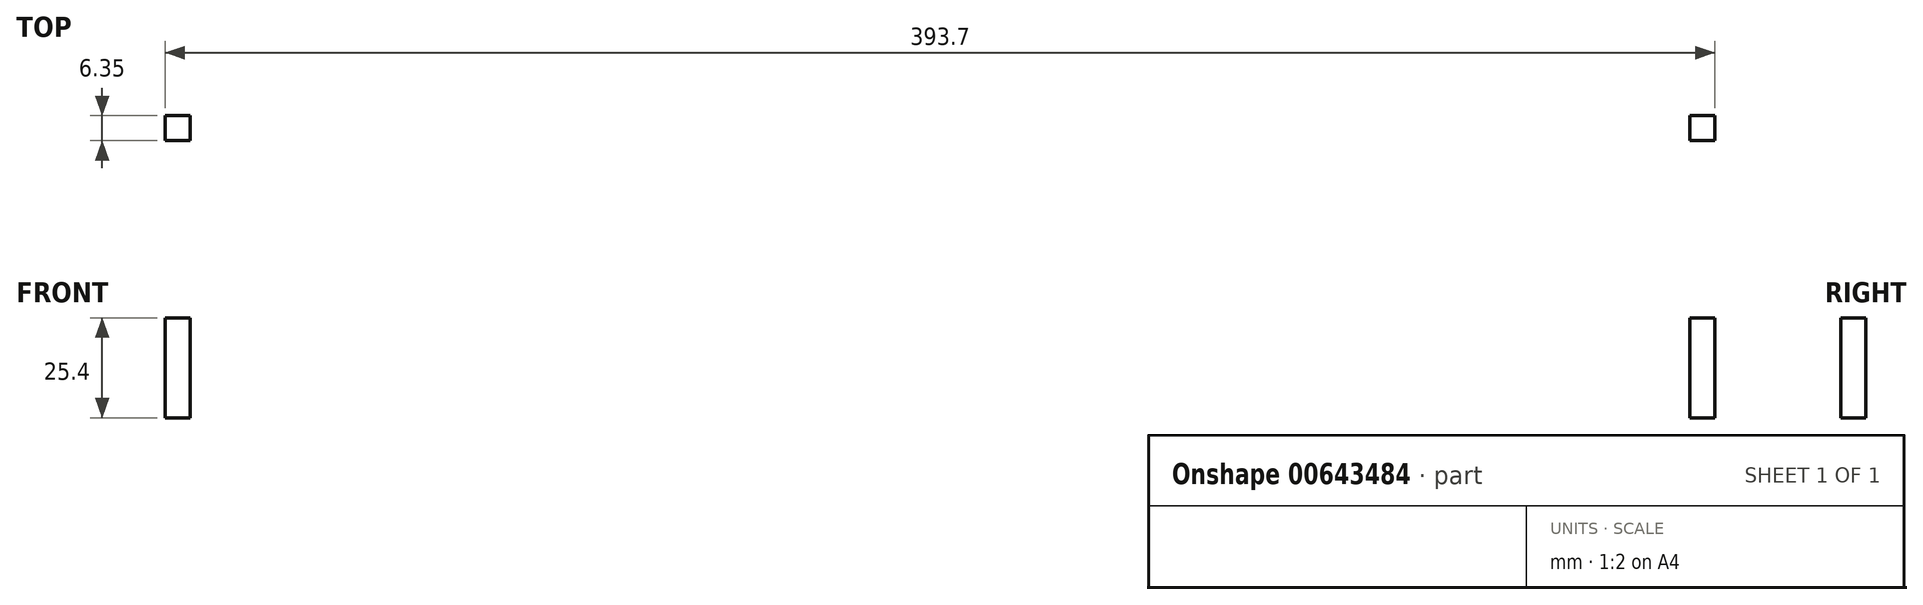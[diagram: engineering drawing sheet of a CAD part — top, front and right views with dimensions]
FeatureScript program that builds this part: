
annotation { "Feature Type Name" : "Feature", "Feature Type Description" : "" }
export const myFeature = defineFeature(function(context is Context, id is Id, definition is map)
    precondition{}
    {
        {
            var Q0;
            Q0=qCreatedBy(makeId("Front.planeOp"),FACE);
            var sketch = newSketch(context, id + "F0", { "sketchPlane" : qUnion([Q0])});
            skLineSegment(sketch, "E0.bottom", {"start": v(-181.53, -108.15) * mm, "end": v(199.47, -108.15) * mm});
            skLineSegment(sketch, "E0.top", {"start": v(-181.53, -44.65) * mm, "end": v(199.47, -44.65) * mm});
            skLineSegment(sketch, "E0.left", {"start": v(-181.53, -108.15) * mm, "end": v(-181.53, -44.65) * mm});
            skLineSegment(sketch, "E0.right", {"start": v(199.47, -108.15) * mm, "end": v(199.47, -44.65) * mm});
            skLineSegment(sketch, "E1.bottom", {"start": v(-181.53, -63.7) * mm, "end": v(-187.88, -63.7) * mm});
            skLineSegment(sketch, "E1.top", {"start": v(-181.53, -89.1) * mm, "end": v(-187.88, -89.1) * mm});
            skLineSegment(sketch, "E1.left", {"start": v(-181.53, -63.7) * mm, "end": v(-181.53, -89.1) * mm});
            skLineSegment(sketch, "E1.right", {"start": v(-187.88, -63.7) * mm, "end": v(-187.88, -89.1) * mm});
            skLineSegment(sketch, "E2.bottom", {"start": v(199.47, -63.7) * mm, "end": v(205.82, -63.7) * mm});
            skLineSegment(sketch, "E2.top", {"start": v(199.47, -89.1) * mm, "end": v(205.82, -89.1) * mm});
            skLineSegment(sketch, "E2.left", {"start": v(199.47, -63.7) * mm, "end": v(199.47, -89.1) * mm});
            skLineSegment(sketch, "E2.right", {"start": v(205.82, -63.7) * mm, "end": v(205.82, -89.1) * mm});
            skLineSegment(sketch, "E3.bottom", {"start": v(-130.73, -108.15) * mm, "end": v(-79.93, -108.15) * mm});
            skLineSegment(sketch, "E3.top", {"start": v(-130.73, -114.5) * mm, "end": v(-79.93, -114.5) * mm});
            skLineSegment(sketch, "E3.left", {"start": v(-130.73, -108.15) * mm, "end": v(-130.73, -114.5) * mm});
            skLineSegment(sketch, "E3.right", {"start": v(-79.93, -108.15) * mm, "end": v(-79.93, -114.5) * mm});
            skLineSegment(sketch, "E4.bottom", {"start": v(97.87, -108.15) * mm, "end": v(148.67, -108.15) * mm});
            skLineSegment(sketch, "E4.top", {"start": v(97.87, -114.5) * mm, "end": v(148.67, -114.5) * mm});
            skLineSegment(sketch, "E4.left", {"start": v(97.87, -108.15) * mm, "end": v(97.87, -114.5) * mm});
            skLineSegment(sketch, "E4.right", {"start": v(148.67, -108.15) * mm, "end": v(148.67, -114.5) * mm});
            skLineSegment(sketch, "E5.bottom", {"start": v(-130.73, -44.65) * mm, "end": v(-79.93, -44.65) * mm});
            skLineSegment(sketch, "E5.top", {"start": v(-130.73, -38.3) * mm, "end": v(-79.93, -38.3) * mm});
            skLineSegment(sketch, "E5.left", {"start": v(-130.73, -44.65) * mm, "end": v(-130.73, -38.3) * mm});
            skLineSegment(sketch, "E5.right", {"start": v(-79.93, -44.65) * mm, "end": v(-79.93, -38.3) * mm});
            skLineSegment(sketch, "E6.bottom", {"start": v(97.87, -44.65) * mm, "end": v(148.67, -44.65) * mm});
            skLineSegment(sketch, "E6.top", {"start": v(97.87, -38.3) * mm, "end": v(148.67, -38.3) * mm});
            skLineSegment(sketch, "E6.left", {"start": v(97.87, -44.65) * mm, "end": v(97.87, -38.3) * mm});
            skLineSegment(sketch, "E6.right", {"start": v(148.67, -44.65) * mm, "end": v(148.67, -38.3) * mm});
            skSolve(sketch);
        }
        {
            var Q0;
            {var subQ8=sQuery(id+"F0.wireOp",EDGE,"E1.left");Q0=makeQuery(id+"F0.imprint","IMPRINT",FACE,{"disambiguationData":[TD([[makeQuery(id+"F0.imprint","IMPRINT",EDGE,{"derivedFrom":subQ8}),1.0]])]});}
            var Q1;
            Q1=makeQuery(id+"F0.imprint","IMPRINT",FACE,{"disambiguationData":[TD([[makeQuery(id+"F0.imprint","IMPRINT",EDGE,{"derivedFrom":sQuery(id+"F0.wireOp",EDGE,"E5.bottom")}),1.0]])]});
            var Q2;
            Q2=makeQuery(id+"F0.imprint","IMPRINT",FACE,{"disambiguationData":[TD([[makeQuery(id+"F0.imprint","IMPRINT",EDGE,{"derivedFrom":sQuery(id+"F0.wireOp",EDGE,"E1.bottom")}),1.0]])]});
            var Q3;
            Q3=makeQuery(id+"F0.imprint","IMPRINT",FACE,{"disambiguationData":[TD([[makeQuery(id+"F0.imprint","IMPRINT",EDGE,{"derivedFrom":sQuery(id+"F0.wireOp",EDGE,"E3.bottom")}),-1.0]])]});
            var Q4;
            Q4=makeQuery(id+"F0.imprint","IMPRINT",FACE,{"disambiguationData":[TD([[makeQuery(id+"F0.imprint","IMPRINT",EDGE,{"derivedFrom":sQuery(id+"F0.wireOp",EDGE,"E4.bottom")}),-1.0]])]});
            var Q5;
            Q5=makeQuery(id+"F0.imprint","IMPRINT",FACE,{"disambiguationData":[TD([[makeQuery(id+"F0.imprint","IMPRINT",EDGE,{"derivedFrom":sQuery(id+"F0.wireOp",EDGE,"E6.bottom")}),1.0]])]});
            var Q6;
            Q6=makeQuery(id+"F0.imprint","IMPRINT",FACE,{"disambiguationData":[TD([[makeQuery(id+"F0.imprint","IMPRINT",EDGE,{"derivedFrom":sQuery(id+"F0.wireOp",EDGE,"E2.bottom")}),-1.0]])]});
            extrude(context, id + "F1", {"entities" : qUnion([Q0, Q1, Q2, Q3, Q4, Q5, Q6]), "depth" : 6.35 * mm, "offsetDistance" : 25.4 * mm});
        }
    });
